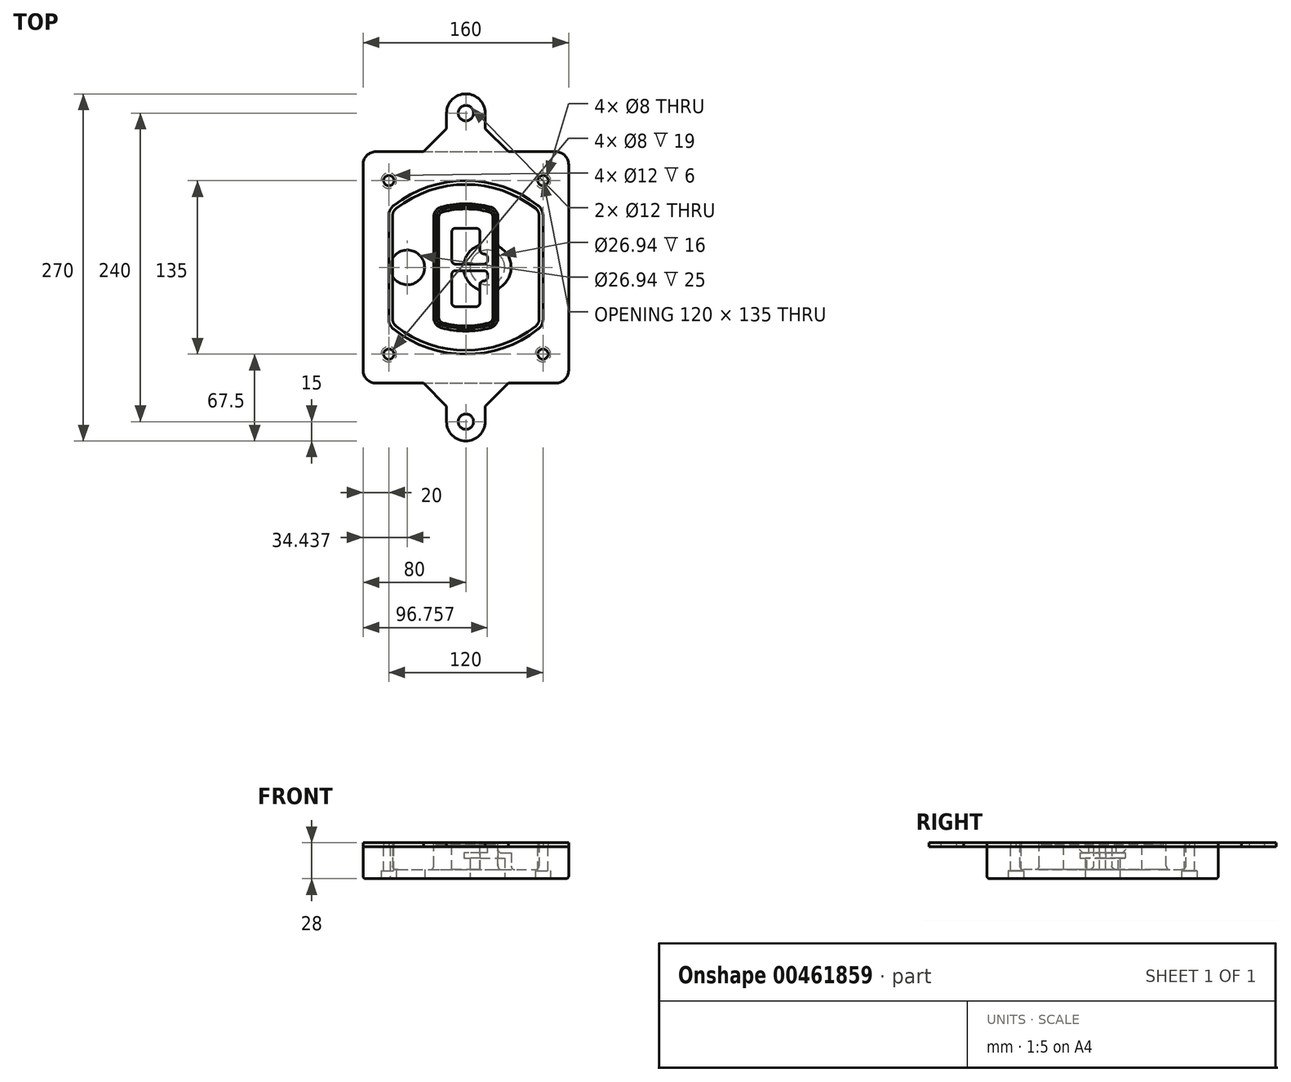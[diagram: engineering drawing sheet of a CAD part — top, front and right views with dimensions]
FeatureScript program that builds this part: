
annotation { "Feature Type Name" : "Feature", "Feature Type Description" : "" }
export const myFeature = defineFeature(function(context is Context, id is Id, definition is map)
    precondition{}
    {
        {
            var Q0;
            Q0=qCreatedBy(makeId("Top.planeOp"),FACE);
            var sketch = newSketch(context, id + "F0", { "sketchPlane" : qUnion([Q0])});
            skPoint(sketch, "E0.rect.middle", {"position": v(0, 0) * mm});
            skLineSegment(sketch, "E1.bottom", {"start": v(-70, -90) * mm, "end": v(70, -90) * mm});
            skLineSegment(sketch, "E1.top", {"start": v(-70, 90) * mm, "end": v(70, 90) * mm});
            skLineSegment(sketch, "E1.left", {"start": v(-80, -80) * mm, "end": v(-80, 80) * mm});
            skLineSegment(sketch, "E1.right", {"start": v(80, -80) * mm, "end": v(80, 80) * mm});
            skLineSegment(sketch, "E2", {"start": v(-80, 90) * mm, "end": v(80, -90) * mm, "construction": true});
            skLineSegment(sketch, "E3", {"start": v(80, 90) * mm, "end": v(-80, -90) * mm, "construction": true});
            skCircle(sketch, "E4", {"center": v(-60, 67.5) * mm, "radius": 4 * mm});
            skCircle(sketch, "E5", {"center": v(60, 67.5) * mm, "radius": 4 * mm});
            skCircle(sketch, "E6", {"center": v(60, -67.5) * mm, "radius": 4 * mm});
            skCircle(sketch, "E7", {"center": v(-60, -67.5) * mm, "radius": 4 * mm});
            skLineSegment(sketch, "E8", {"start": v(-60, 67.5) * mm, "end": v(60, 67.5) * mm, "construction": true});
            skLineSegment(sketch, "E9", {"start": v(60, 67.5) * mm, "end": v(60, -67.5) * mm, "construction": true});
            skLineSegment(sketch, "E10", {"start": v(60, -67.5) * mm, "end": v(-60, -67.5) * mm, "construction": true});
            skLineSegment(sketch, "E11", {"start": v(-60, -67.5) * mm, "end": v(-60, 67.5) * mm, "construction": true});
            skLineSegment(sketch, "E12", {"start": v(-60, 40.3) * mm, "end": v(-60, -40.3) * mm});
            skLineSegment(sketch, "E13", {"start": v(60, 40.3) * mm, "end": v(60, -40.3) * mm});
            skArc(sketch, "E14", {"start": v(56.15, 48.18) * mm, "mid": v(0, 67.5) * mm, "end": v(-56.15, 48.18) * mm});
            skArc(sketch, "E15", {"start": v(-56.15, -48.18) * mm, "mid": v(0, -67.5) * mm, "end": v(56.15, -48.18) * mm});
            skLineSegment(sketch, "E16", {"start": v(-60, 0) * mm, "end": v(60, 0) * mm, "construction": true});
            skPoint(sketch, "E17.visualSharp", {"position": v(-60, -45) * mm});
            skArc(sketch, "E17.filletArc", {"start": v(-60, -40.3) * mm, "mid": v(-58.99, -44.68) * mm, "end": v(-56.15, -48.18) * mm});
            skPoint(sketch, "E18.visualSharp", {"position": v(-60, 45) * mm});
            skArc(sketch, "E18.filletArc", {"start": v(-56.15, 48.18) * mm, "mid": v(-58.99, 44.68) * mm, "end": v(-60, 40.3) * mm});
            skPoint(sketch, "E19.visualSharp", {"position": v(60, 45) * mm});
            skArc(sketch, "E19.filletArc", {"start": v(60, 40.3) * mm, "mid": v(58.99, 44.68) * mm, "end": v(56.15, 48.18) * mm});
            skPoint(sketch, "E20.visualSharp", {"position": v(60, -45) * mm});
            skArc(sketch, "E20.filletArc", {"start": v(56.15, -48.18) * mm, "mid": v(58.99, -44.68) * mm, "end": v(60, -40.3) * mm});
            skPoint(sketch, "E21.visualSharp", {"position": v(-80, 90) * mm});
            skArc(sketch, "E21.filletArc", {"start": v(-70, 90) * mm, "mid": v(-77.07, 87.07) * mm, "end": v(-80, 80) * mm});
            skPoint(sketch, "E22.visualSharp", {"position": v(80, 90) * mm});
            skArc(sketch, "E22.filletArc", {"start": v(80, 80) * mm, "mid": v(77.07, 87.07) * mm, "end": v(70, 90) * mm});
            skPoint(sketch, "E23.visualSharp", {"position": v(80, -90) * mm});
            skArc(sketch, "E23.filletArc", {"start": v(70, -90) * mm, "mid": v(77.07, -87.07) * mm, "end": v(80, -80) * mm});
            skPoint(sketch, "E24.visualSharp", {"position": v(-80, -90) * mm});
            skArc(sketch, "E24.filletArc", {"start": v(-80, -80) * mm, "mid": v(-77.07, -87.07) * mm, "end": v(-70, -90) * mm});
            skArc(sketch, "E25.0", {"start": v(57, 40.3) * mm, "mid": v(56.3, 43.36) * mm, "end": v(54.3, 45.81) * mm});
            skLineSegment(sketch, "E25.1", {"start": v(57, 40.3) * mm, "end": v(57, -40.3) * mm});
            skArc(sketch, "E25.2", {"start": v(54.3, -45.81) * mm, "mid": v(56.3, -43.36) * mm, "end": v(57, -40.3) * mm});
            skArc(sketch, "E25.3", {"start": v(-54.3, -45.81) * mm, "mid": v(0, -64.5) * mm, "end": v(54.3, -45.81) * mm});
            skArc(sketch, "E25.4", {"start": v(-57, -40.3) * mm, "mid": v(-56.3, -43.36) * mm, "end": v(-54.3, -45.81) * mm});
            skArc(sketch, "E25.5", {"start": v(54.3, 45.81) * mm, "mid": v(0, 64.5) * mm, "end": v(-54.3, 45.81) * mm});
            skLineSegment(sketch, "E25.6", {"start": v(-57, 40.3) * mm, "end": v(-57, -40.3) * mm});
            skArc(sketch, "E25.7", {"start": v(-54.3, 45.81) * mm, "mid": v(-56.3, 43.36) * mm, "end": v(-57, 40.3) * mm});
            skArc(sketch, "E26.0", {"start": v(-58.62, 51.33) * mm, "mid": v(-62.58, 46.43) * mm, "end": v(-64, 40.3) * mm});
            skArc(sketch, "E26.1", {"start": v(58.62, 51.33) * mm, "mid": v(0, 71.5) * mm, "end": v(-58.62, 51.33) * mm});
            skArc(sketch, "E26.2", {"start": v(64, 40.3) * mm, "mid": v(62.58, 46.43) * mm, "end": v(58.62, 51.33) * mm});
            skLineSegment(sketch, "E26.3", {"start": v(64, 40.3) * mm, "end": v(64, -40.3) * mm});
            skArc(sketch, "E26.4", {"start": v(58.62, -51.33) * mm, "mid": v(62.58, -46.43) * mm, "end": v(64, -40.3) * mm});
            skLineSegment(sketch, "E26.5", {"start": v(-64, 40.3) * mm, "end": v(-64, -40.3) * mm});
            skArc(sketch, "E26.6", {"start": v(-58.62, -51.33) * mm, "mid": v(0, -71.5) * mm, "end": v(58.62, -51.33) * mm});
            skArc(sketch, "E26.7", {"start": v(-64, -40.3) * mm, "mid": v(-62.58, -46.43) * mm, "end": v(-58.62, -51.33) * mm});
            skSolve(sketch);
        }
        {
            var Q0;
            Q0=makeQuery(id+"F0.imprint","IMPRINT",FACE,{"disambiguationData":[TD([[makeQuery(id+"F0.imprint","IMPRINT",EDGE,{"derivedFrom":sQuery(id+"F0.wireOp",EDGE,"E1.bottom")}),1.0]])]});
            var Q1;
            Q1=makeQuery(id+"F0.imprint","IMPRINT",FACE,{"disambiguationData":[TD([[makeQuery(id+"F0.imprint","IMPRINT",EDGE,{"derivedFrom":sQuery(id+"F0.wireOp",EDGE,"E12")}),1.0]])]});
            var Q2;
            Q2=makeQuery(id+"F0.imprint","IMPRINT",FACE,{"disambiguationData":[TD([[makeQuery(id+"F0.imprint","IMPRINT",EDGE,{"derivedFrom":sQuery(id+"F0.wireOp",EDGE,"E25.0")}),1.0]])]});
            var Q3;
            Q3=makeQuery(id+"F0.imprint","IMPRINT",FACE,{"disambiguationData":[TD([[makeQuery(id+"F0.imprint","IMPRINT",EDGE,{"derivedFrom":sQuery(id+"F0.wireOp",EDGE,"E12")}),-1.0]])]});
            extrude(context, id + "F1", {"entities" : qUnion([Q0, Q1, Q2, Q3]), "oppositeDirection" : true, "depth" : 25 * mm});
        }
        {
            var Q0;
            Q0=makeQuery(id+"F0.imprint","IMPRINT",FACE,{"disambiguationData":[TD([[makeQuery(id+"F0.imprint","IMPRINT",EDGE,{"derivedFrom":sQuery(id+"F0.wireOp",EDGE,"E12")}),1.0]])]});
            extrude(context, id + "F2", {"entities" : qUnion([Q0]), "operationType" : NewBodyOperationType.ADD, "depth" : 3 * mm});
        }
        {
            var Q0;
            Q0=makeQuery(id+"F0.imprint","IMPRINT",FACE,{"disambiguationData":[TD([[makeQuery(id+"F0.imprint","IMPRINT",EDGE,{"derivedFrom":sQuery(id+"F0.wireOp",EDGE,"E25.0")}),1.0]])]});
            extrude(context, id + "F3", {"entities" : qUnion([Q0]), "operationType" : NewBodyOperationType.REMOVE, "oppositeDirection" : true, "depth" : 18 * mm});
        }
        {
            var Q0;
            Q0=makeQuery(id+"F2.opExtrude","CAP_FACE",FACE,{"disambiguationData":[OSD([sQuery(id+"F0.wireOp",EDGE,"E12"),sQuery(id+"F0.wireOp",EDGE,"E13"),sQuery(id+"F0.wireOp",EDGE,"E14"),sQuery(id+"F0.wireOp",EDGE,"E15"),sQuery(id+"F0.wireOp",EDGE,"E17.filletArc"),sQuery(id+"F0.wireOp",EDGE,"E18.filletArc"),sQuery(id+"F0.wireOp",EDGE,"E19.filletArc"),sQuery(id+"F0.wireOp",EDGE,"E20.filletArc"),sQuery(id+"F0.wireOp",EDGE,"E25.0"),sQuery(id+"F0.wireOp",EDGE,"E25.1"),sQuery(id+"F0.wireOp",EDGE,"E25.2"),sQuery(id+"F0.wireOp",EDGE,"E25.3"),sQuery(id+"F0.wireOp",EDGE,"E25.4"),sQuery(id+"F0.wireOp",EDGE,"E25.5"),sQuery(id+"F0.wireOp",EDGE,"E25.6"),sQuery(id+"F0.wireOp",EDGE,"E25.7")])],"isStart":false});
            var sketch = newSketch(context, id + "F4", { "sketchPlane" : qUnion([Q0])});
            skArc(sketch, "E27.0", {"start": v(-19.08, -46.97) * mm, "mid": v(0, -49.5) * mm, "end": v(19.08, -46.97) * mm});
            skArc(sketch, "E28.0", {"start": v(19.08, 46.97) * mm, "mid": v(0, 49.5) * mm, "end": v(-19.08, 46.97) * mm});
            skLineSegment(sketch, "E29", {"start": v(-25, 39.25) * mm, "end": v(-25, -39.25) * mm});
            skLineSegment(sketch, "E30", {"start": v(25, 39.25) * mm, "end": v(25, -39.25) * mm});
            skLineSegment(sketch, "E31", {"start": v(-25, 45.1) * mm, "end": v(25, 45.1) * mm, "construction": true});
            skLineSegment(sketch, "E32", {"start": v(-25, -45.1) * mm, "end": v(25, -45.1) * mm, "construction": true});
            skPoint(sketch, "E33.visualSharp", {"position": v(-25, 45.1) * mm});
            skArc(sketch, "E33.filletArc", {"start": v(-19.08, 46.97) * mm, "mid": v(-23.35, 44.11) * mm, "end": v(-25, 39.25) * mm});
            skPoint(sketch, "E34.visualSharp", {"position": v(25, 45.1) * mm});
            skArc(sketch, "E34.filletArc", {"start": v(25, 39.25) * mm, "mid": v(23.35, 44.11) * mm, "end": v(19.08, 46.97) * mm});
            skPoint(sketch, "E35.visualSharp", {"position": v(25, -45.1) * mm});
            skArc(sketch, "E35.filletArc", {"start": v(19.08, -46.97) * mm, "mid": v(23.35, -44.11) * mm, "end": v(25, -39.25) * mm});
            skPoint(sketch, "E36.visualSharp", {"position": v(-25, -45.1) * mm});
            skArc(sketch, "E36.filletArc", {"start": v(-25, -39.25) * mm, "mid": v(-23.35, -44.11) * mm, "end": v(-19.08, -46.97) * mm});
            skArc(sketch, "E37.0", {"start": v(54.3, 45.81) * mm, "mid": v(0, 64.5) * mm, "end": v(-54.3, 45.81) * mm});
            skArc(sketch, "E37.1", {"start": v(-54.3, 45.81) * mm, "mid": v(-56.3, 43.36) * mm, "end": v(-57, 40.3) * mm});
            skLineSegment(sketch, "E37.2", {"start": v(-57, 40.3) * mm, "end": v(-57, -40.3) * mm});
            skArc(sketch, "E37.3", {"start": v(-57, -40.3) * mm, "mid": v(-56.3, -43.36) * mm, "end": v(-54.3, -45.81) * mm});
            skArc(sketch, "E37.4", {"start": v(-54.3, -45.81) * mm, "mid": v(0, -64.5) * mm, "end": v(54.3, -45.81) * mm});
            skArc(sketch, "E37.5", {"start": v(54.3, -45.81) * mm, "mid": v(56.3, -43.36) * mm, "end": v(57, -40.3) * mm});
            skLineSegment(sketch, "E37.6", {"start": v(57, 40.3) * mm, "end": v(57, -40.3) * mm});
            skArc(sketch, "E37.7", {"start": v(57, 40.3) * mm, "mid": v(56.3, 43.36) * mm, "end": v(54.3, 45.81) * mm});
            skLineSegment(sketch, "E38.0", {"start": v(23, 39.25) * mm, "end": v(23, -39.25) * mm});
            skArc(sketch, "E38.1", {"start": v(18.56, -45.04) * mm, "mid": v(21.76, -42.9) * mm, "end": v(23, -39.25) * mm});
            skArc(sketch, "E38.2", {"start": v(-18.56, -45.04) * mm, "mid": v(0, -47.5) * mm, "end": v(18.56, -45.04) * mm});
            skArc(sketch, "E38.3", {"start": v(-23, -39.25) * mm, "mid": v(-21.76, -42.9) * mm, "end": v(-18.56, -45.04) * mm});
            skLineSegment(sketch, "E38.4", {"start": v(-23, 39.25) * mm, "end": v(-23, -39.25) * mm});
            skArc(sketch, "E38.5", {"start": v(23, 39.25) * mm, "mid": v(21.76, 42.9) * mm, "end": v(18.56, 45.04) * mm});
            skArc(sketch, "E38.6", {"start": v(-18.56, 45.04) * mm, "mid": v(-21.76, 42.9) * mm, "end": v(-23, 39.25) * mm});
            skArc(sketch, "E38.7", {"start": v(18.56, 45.04) * mm, "mid": v(0, 47.5) * mm, "end": v(-18.56, 45.04) * mm});
            skArc(sketch, "E39.0", {"start": v(21, 39.25) * mm, "mid": v(20.18, 41.68) * mm, "end": v(18.04, 43.1) * mm});
            skLineSegment(sketch, "E39.1", {"start": v(21, 39.25) * mm, "end": v(21, -39.25) * mm});
            skArc(sketch, "E39.2", {"start": v(18.04, -43.1) * mm, "mid": v(20.18, -41.68) * mm, "end": v(21, -39.25) * mm});
            skArc(sketch, "E39.3", {"start": v(-18.04, -43.1) * mm, "mid": v(0, -45.5) * mm, "end": v(18.04, -43.1) * mm});
            skArc(sketch, "E39.4", {"start": v(-21, -39.25) * mm, "mid": v(-20.18, -41.68) * mm, "end": v(-18.04, -43.1) * mm});
            skArc(sketch, "E39.5", {"start": v(18.04, 43.1) * mm, "mid": v(0, 45.5) * mm, "end": v(-18.04, 43.1) * mm});
            skLineSegment(sketch, "E39.6", {"start": v(-21, 39.25) * mm, "end": v(-21, -39.25) * mm});
            skArc(sketch, "E39.7", {"start": v(-18.04, 43.1) * mm, "mid": v(-20.18, 41.68) * mm, "end": v(-21, 39.25) * mm});
            skLineSegment(sketch, "E40", {"start": v(-25, 0) * mm, "end": v(25, 0) * mm, "construction": true});
            skLineSegment(sketch, "E41", {"start": v(-11, 5.5) * mm, "end": v(-11, 27.5) * mm});
            skLineSegment(sketch, "E42", {"start": v(-8, 30.5) * mm, "end": v(8, 30.5) * mm});
            skLineSegment(sketch, "E43", {"start": v(11, 27.5) * mm, "end": v(11, 13.5) * mm});
            skLineSegment(sketch, "E44", {"start": v(14, 10.5) * mm, "end": v(14, 10.5) * mm});
            skLineSegment(sketch, "E45", {"start": v(17, 7.5) * mm, "end": v(17, 5.5) * mm});
            skLineSegment(sketch, "E46", {"start": v(14, 2.5) * mm, "end": v(-8, 2.5) * mm});
            skPoint(sketch, "E47.visualSharp", {"position": v(-11, 30.5) * mm});
            skArc(sketch, "E47.filletArc", {"start": v(-8, 30.5) * mm, "mid": v(-10.12, 29.62) * mm, "end": v(-11, 27.5) * mm});
            skPoint(sketch, "E48.visualSharp", {"position": v(11, 30.5) * mm});
            skArc(sketch, "E48.filletArc", {"start": v(11, 27.5) * mm, "mid": v(10.12, 29.62) * mm, "end": v(8, 30.5) * mm});
            skPoint(sketch, "E49.visualSharp", {"position": v(11, 10.5) * mm});
            skArc(sketch, "E49.filletArc", {"start": v(11, 13.5) * mm, "mid": v(11.88, 11.38) * mm, "end": v(14, 10.5) * mm});
            skPoint(sketch, "E50.visualSharp", {"position": v(17, 10.5) * mm});
            skArc(sketch, "E50.filletArc", {"start": v(17, 7.5) * mm, "mid": v(16.12, 9.62) * mm, "end": v(14, 10.5) * mm});
            skPoint(sketch, "E51.visualSharp", {"position": v(17, 2.5) * mm});
            skArc(sketch, "E51.filletArc", {"start": v(14, 2.5) * mm, "mid": v(16.12, 3.38) * mm, "end": v(17, 5.5) * mm});
            skPoint(sketch, "E52.visualSharp", {"position": v(-11, 2.5) * mm});
            skArc(sketch, "E52.filletArc", {"start": v(-11, 5.5) * mm, "mid": v(-10.12, 3.38) * mm, "end": v(-8, 2.5) * mm});
            skLineSegment(sketch, "E53.0.MirrorCS", {"start": v(14, -2.5) * mm, "end": v(-8, -2.5) * mm});
            skArc(sketch, "E54.0.MirrorCS", {"start": v(-11, -5.5) * mm, "mid": v(-10.12, -3.38) * mm, "end": v(-8, -2.5) * mm});
            skLineSegment(sketch, "E55.0.MirrorCS", {"start": v(-11, -5.5) * mm, "end": v(-11, -27.5) * mm});
            skArc(sketch, "E56.0.MirrorCS", {"start": v(-8, -30.5) * mm, "mid": v(-10.12, -29.62) * mm, "end": v(-11, -27.5) * mm});
            skLineSegment(sketch, "E57.0.MirrorCS", {"start": v(-8, -30.5) * mm, "end": v(8, -30.5) * mm});
            skArc(sketch, "E58.0.MirrorCS", {"start": v(11, -27.5) * mm, "mid": v(10.12, -29.62) * mm, "end": v(8, -30.5) * mm});
            skLineSegment(sketch, "E59.0.MirrorCS", {"start": v(11, -27.5) * mm, "end": v(11, -13.5) * mm});
            skArc(sketch, "E60.0.MirrorCS", {"start": v(11, -13.5) * mm, "mid": v(11.88, -11.38) * mm, "end": v(14, -10.5) * mm});
            skArc(sketch, "E61.0.MirrorCS", {"start": v(17, -7.5) * mm, "mid": v(16.12, -9.62) * mm, "end": v(14, -10.5) * mm});
            skLineSegment(sketch, "E62.0.MirrorCS", {"start": v(17, -7.5) * mm, "end": v(17, -5.5) * mm});
            skArc(sketch, "E63.0.MirrorCS", {"start": v(14, -2.5) * mm, "mid": v(16.12, -3.38) * mm, "end": v(17, -5.5) * mm});
            skSolve(sketch);
        }
        {
            var Q0;
            Q0=makeQuery(id+"F4.imprint","IMPRINT",FACE,{"disambiguationData":[TD([[makeQuery(id+"F4.imprint","IMPRINT",EDGE,{"derivedFrom":sQuery(id+"F4.wireOp",EDGE,"E27.0")}),1.0]])]});
            var Q1;
            Q1=makeQuery(id+"F4.imprint","IMPRINT",FACE,{"disambiguationData":[TD([[makeQuery(id+"F4.imprint","IMPRINT",EDGE,{"derivedFrom":sQuery(id+"F4.wireOp",EDGE,"E38.0")}),-1.0]])]});
            var Q2;
            Q2=makeQuery(id+"F4.imprint","IMPRINT",FACE,{"disambiguationData":[TD([[makeQuery(id+"F4.imprint","IMPRINT",EDGE,{"derivedFrom":sQuery(id+"F4.wireOp",EDGE,"E39.0")}),1.0]])]});
            extrude(context, id + "F5", {"entities" : qUnion([Q0, Q1, Q2]), "operationType" : NewBodyOperationType.ADD, "endBound" : BoundingType.UP_TO_NEXT, "oppositeDirection" : true, "depth" : 25 * mm});
        }
        {
            var Q0;
            Q0=makeQuery(id+"F4.imprint","IMPRINT",FACE,{"disambiguationData":[TD([[makeQuery(id+"F4.imprint","IMPRINT",EDGE,{"derivedFrom":sQuery(id+"F4.wireOp",EDGE,"E38.0")}),-1.0]])]});
            extrude(context, id + "F6", {"entities" : qUnion([Q0]), "operationType" : NewBodyOperationType.REMOVE, "oppositeDirection" : true, "depth" : 2 * mm});
        }
        {
            var Q0;
            Q0=makeQuery(id+"F1.opExtrude","CAP_FACE",FACE,{"disambiguationData":[OSD([sQuery(id+"F0.wireOp",EDGE,"E1.bottom"),sQuery(id+"F0.wireOp",EDGE,"E1.top"),sQuery(id+"F0.wireOp",EDGE,"E1.left"),sQuery(id+"F0.wireOp",EDGE,"E1.right"),sQuery(id+"F0.wireOp",EDGE,"E4"),sQuery(id+"F0.wireOp",EDGE,"E5"),sQuery(id+"F0.wireOp",EDGE,"E6"),sQuery(id+"F0.wireOp",EDGE,"E7"),sQuery(id+"F0.wireOp",EDGE,"E21.filletArc"),sQuery(id+"F0.wireOp",EDGE,"E22.filletArc"),sQuery(id+"F0.wireOp",EDGE,"E23.filletArc"),sQuery(id+"F0.wireOp",EDGE,"E24.filletArc")])],"isStart":false});
            var sketch = newSketch(context, id + "F7", { "sketchPlane" : qUnion([Q0])});
            skCircle(sketch, "E64", {"center": v(16.76, 0) * mm, "radius": 13.47 * mm});
            skCircle(sketch, "E65", {"center": v(-45.56, 0) * mm, "radius": 13.47 * mm});
            skLineSegment(sketch, "E66", {"start": v(80, 0) * mm, "end": v(-80, 0) * mm});
            skCircle(sketch, "E67", {"center": v(16.76, 0) * mm, "radius": 18.47 * mm});
            skCircle(sketch, "E68", {"center": v(60, -67.5) * mm, "radius": 6 * mm});
            skCircle(sketch, "E69", {"center": v(-60, -67.5) * mm, "radius": 6 * mm});
            skCircle(sketch, "E70", {"center": v(-60, 67.5) * mm, "radius": 6 * mm});
            skCircle(sketch, "E71", {"center": v(60, 67.5) * mm, "radius": 6 * mm});
            skSolve(sketch);
        }
        {
            var Q0;
            {var subQ1=sQuery(id+"F7.wireOp",EDGE,"E66");var subQ4=sQuery(id+"F7.wireOp",EDGE,"E64");var subQ6=makeQuery(id+"F7.imprint","INTERSECT",VERTEX,{"disambiguationData":[OD(0.0)],"derivedFrom":[subQ4,subQ1]});Q0=makeQuery(id+"F7.imprint","IMPRINT",FACE,{"disambiguationData":[TD([[makeQuery(id+"F7.imprint","IMPRINT",EDGE,{"disambiguationData":[TD([[subQ6,-1.0]])],"derivedFrom":subQ4}),-1.0]])]});}
            var Q1;
            {var subQ0=sQuery(id+"F7.wireOp",EDGE,"E66");var subQ1=sQuery(id+"F7.wireOp",EDGE,"E64");var subQ3=makeQuery(id+"F7.imprint","INTERSECT",VERTEX,{"disambiguationData":[OD(0.0)],"derivedFrom":[subQ1,subQ0]});Q1=makeQuery(id+"F7.imprint","IMPRINT",FACE,{"disambiguationData":[TD([[makeQuery(id+"F7.imprint","IMPRINT",EDGE,{"disambiguationData":[TD([[subQ3,-1.0]])],"derivedFrom":subQ1}),1.0]])]});}
            var Q2;
            {var subQ0=sQuery(id+"F7.wireOp",EDGE,"E66");var subQ1=sQuery(id+"F7.wireOp",EDGE,"E64");var subQ3=makeQuery(id+"F7.imprint","INTERSECT",VERTEX,{"disambiguationData":[OD(0.0)],"derivedFrom":[subQ1,subQ0]});Q2=makeQuery(id+"F7.imprint","IMPRINT",FACE,{"disambiguationData":[TD([[makeQuery(id+"F7.imprint","IMPRINT",EDGE,{"disambiguationData":[TD([[subQ3,1.0]])],"derivedFrom":subQ1}),1.0]])]});}
            var Q3;
            {var subQ1=sQuery(id+"F7.wireOp",EDGE,"E66");var subQ4=sQuery(id+"F7.wireOp",EDGE,"E64");var subQ6=makeQuery(id+"F7.imprint","INTERSECT",VERTEX,{"disambiguationData":[OD(0.0)],"derivedFrom":[subQ4,subQ1]});Q3=makeQuery(id+"F7.imprint","IMPRINT",FACE,{"disambiguationData":[TD([[makeQuery(id+"F7.imprint","IMPRINT",EDGE,{"disambiguationData":[TD([[subQ6,1.0]])],"derivedFrom":subQ4}),-1.0]])]});}
            extrude(context, id + "F8", {"entities" : qUnion([Q0, Q1, Q2, Q3]), "operationType" : NewBodyOperationType.ADD, "oppositeDirection" : true, "depth" : 20 * mm});
        }
        {
            var Q0;
            {var subQ0=sQuery(id+"F7.wireOp",EDGE,"E66");var subQ1=sQuery(id+"F7.wireOp",EDGE,"E64");var subQ3=makeQuery(id+"F7.imprint","INTERSECT",VERTEX,{"disambiguationData":[OD(0.0)],"derivedFrom":[subQ1,subQ0]});Q0=makeQuery(id+"F7.imprint","IMPRINT",FACE,{"disambiguationData":[TD([[makeQuery(id+"F7.imprint","IMPRINT",EDGE,{"disambiguationData":[TD([[subQ3,-1.0]])],"derivedFrom":subQ1}),1.0]])]});}
            var Q1;
            {var subQ0=sQuery(id+"F7.wireOp",EDGE,"E66");var subQ1=sQuery(id+"F7.wireOp",EDGE,"E64");var subQ3=makeQuery(id+"F7.imprint","INTERSECT",VERTEX,{"disambiguationData":[OD(0.0)],"derivedFrom":[subQ1,subQ0]});Q1=makeQuery(id+"F7.imprint","IMPRINT",FACE,{"disambiguationData":[TD([[makeQuery(id+"F7.imprint","IMPRINT",EDGE,{"disambiguationData":[TD([[subQ3,1.0]])],"derivedFrom":subQ1}),1.0]])]});}
            extrude(context, id + "F9", {"entities" : qUnion([Q0, Q1]), "operationType" : NewBodyOperationType.REMOVE, "oppositeDirection" : true, "depth" : 16 * mm});
        }
        {
            var Q0;
            {var subQ0=sQuery(id+"F7.wireOp",EDGE,"E66");var subQ1=sQuery(id+"F7.wireOp",EDGE,"E65");var subQ3=makeQuery(id+"F7.imprint","INTERSECT",VERTEX,{"disambiguationData":[OD(0.0)],"derivedFrom":[subQ1,subQ0]});Q0=makeQuery(id+"F7.imprint","IMPRINT",FACE,{"disambiguationData":[TD([[makeQuery(id+"F7.imprint","IMPRINT",EDGE,{"disambiguationData":[TD([[subQ3,-1.0]])],"derivedFrom":subQ1}),1.0]])]});}
            var Q1;
            {var subQ0=sQuery(id+"F7.wireOp",EDGE,"E66");var subQ1=sQuery(id+"F7.wireOp",EDGE,"E65");var subQ3=makeQuery(id+"F7.imprint","INTERSECT",VERTEX,{"disambiguationData":[OD(0.0)],"derivedFrom":[subQ1,subQ0]});Q1=makeQuery(id+"F7.imprint","IMPRINT",FACE,{"disambiguationData":[TD([[makeQuery(id+"F7.imprint","IMPRINT",EDGE,{"disambiguationData":[TD([[subQ3,1.0]])],"derivedFrom":subQ1}),1.0]])]});}
            extrude(context, id + "F10", {"entities" : qUnion([Q0, Q1]), "operationType" : NewBodyOperationType.REMOVE, "oppositeDirection" : true, "depth" : 25 * mm});
        }
        {
            var Q0;
            Q0=makeQuery(id+"F7.imprint","IMPRINT",FACE,{"disambiguationData":[TD([[makeQuery(id+"F7.imprint","IMPRINT",EDGE,{"derivedFrom":sQuery(id+"F7.wireOp",EDGE,"E68")}),1.0]])]});
            var Q1;
            Q1=makeQuery(id+"F7.imprint","IMPRINT",FACE,{"disambiguationData":[TD([[makeQuery(id+"F7.imprint","IMPRINT",EDGE,{"derivedFrom":makeQuery(id+"F1.opExtrude","CAP_EDGE",EDGE,{"disambiguationData":[OSD([sQuery(id+"F0.wireOp",EDGE,"E5")])],"isStart":false})}),-1.0]])]});
            var Q2;
            Q2=makeQuery(id+"F7.imprint","IMPRINT",FACE,{"disambiguationData":[TD([[makeQuery(id+"F7.imprint","IMPRINT",EDGE,{"derivedFrom":sQuery(id+"F7.wireOp",EDGE,"E69")}),1.0]])]});
            var Q3;
            Q3=makeQuery(id+"F7.imprint","IMPRINT",FACE,{"disambiguationData":[TD([[makeQuery(id+"F7.imprint","IMPRINT",EDGE,{"derivedFrom":makeQuery(id+"F1.opExtrude","CAP_EDGE",EDGE,{"disambiguationData":[OSD([sQuery(id+"F0.wireOp",EDGE,"E4")])],"isStart":false})}),-1.0]])]});
            var Q4;
            Q4=makeQuery(id+"F7.imprint","IMPRINT",FACE,{"disambiguationData":[TD([[makeQuery(id+"F7.imprint","IMPRINT",EDGE,{"derivedFrom":sQuery(id+"F7.wireOp",EDGE,"E70")}),1.0]])]});
            var Q5;
            Q5=makeQuery(id+"F7.imprint","IMPRINT",FACE,{"disambiguationData":[TD([[makeQuery(id+"F7.imprint","IMPRINT",EDGE,{"derivedFrom":makeQuery(id+"F1.opExtrude","CAP_EDGE",EDGE,{"disambiguationData":[OSD([sQuery(id+"F0.wireOp",EDGE,"E7")])],"isStart":false})}),-1.0]])]});
            var Q6;
            Q6=makeQuery(id+"F7.imprint","IMPRINT",FACE,{"disambiguationData":[TD([[makeQuery(id+"F7.imprint","IMPRINT",EDGE,{"derivedFrom":sQuery(id+"F7.wireOp",EDGE,"E71")}),1.0]])]});
            var Q7;
            Q7=makeQuery(id+"F7.imprint","IMPRINT",FACE,{"disambiguationData":[TD([[makeQuery(id+"F7.imprint","IMPRINT",EDGE,{"derivedFrom":makeQuery(id+"F1.opExtrude","CAP_EDGE",EDGE,{"disambiguationData":[OSD([sQuery(id+"F0.wireOp",EDGE,"E6")])],"isStart":false})}),-1.0]])]});
            extrude(context, id + "F11", {"entities" : qUnion([Q0, Q1, Q2, Q3, Q4, Q5, Q6, Q7]), "operationType" : NewBodyOperationType.REMOVE, "oppositeDirection" : true, "depth" : 6 * mm});
        }
        {
            var Q0;
            Q0=makeQuery(id+"F9.boolean.opBoolean","COPY",FACE,{"derivedFrom":makeQuery(id+"F9.opExtrude","CAP_FACE",FACE,{"disambiguationData":[OSD([sQuery(id+"F7.wireOp",EDGE,"E64")])],"isStart":false})});
            var sketch = newSketch(context, id + "F12", { "sketchPlane" : qUnion([Q0])});
            skArc(sketch, "E72.0", {"start": v(11, 17.55) * mm, "mid": v(2.57, 11.82) * mm, "end": v(-1.54, 2.5) * mm});
            skArc(sketch, "E72.1", {"start": v(-1.54, -2.5) * mm, "mid": v(2.57, -11.82) * mm, "end": v(11, -17.55) * mm});
            skLineSegment(sketch, "E73", {"start": v(-1.54, -2.5) * mm, "end": v(14, -2.5) * mm});
            skLineSegment(sketch, "E74.0", {"start": v(14, 2.5) * mm, "end": v(-1.54, 2.5) * mm});
            skArc(sketch, "E74.1", {"start": v(14, 2.5) * mm, "mid": v(16.12, 3.38) * mm, "end": v(17, 5.5) * mm});
            skLineSegment(sketch, "E74.2", {"start": v(17, 7.5) * mm, "end": v(17, 5.5) * mm});
            skArc(sketch, "E74.3", {"start": v(17, 7.5) * mm, "mid": v(16.12, 9.62) * mm, "end": v(14, 10.5) * mm});
            skArc(sketch, "E74.4", {"start": v(11, 13.5) * mm, "mid": v(11.88, 11.38) * mm, "end": v(14, 10.5) * mm});
            skLineSegment(sketch, "E74.5", {"start": v(11, 17.55) * mm, "end": v(11, 13.5) * mm});
            skLineSegment(sketch, "E74.7", {"start": v(14, -2.5) * mm, "end": v(-1.54, -2.5) * mm});
            skArc(sketch, "E74.8", {"start": v(14, -2.5) * mm, "mid": v(16.12, -3.38) * mm, "end": v(17, -5.5) * mm});
            skLineSegment(sketch, "E74.9", {"start": v(17, -7.5) * mm, "end": v(17, -5.5) * mm});
            skArc(sketch, "E74.10", {"start": v(17, -7.5) * mm, "mid": v(16.12, -9.62) * mm, "end": v(14, -10.5) * mm});
            skArc(sketch, "E74.11", {"start": v(11, -13.5) * mm, "mid": v(11.88, -11.38) * mm, "end": v(14, -10.5) * mm});
            skLineSegment(sketch, "E74.12", {"start": v(11, -17.55) * mm, "end": v(11, -13.5) * mm});
            skPoint(sketch, "E75.orphan", {"position": v(11, -27.5) * mm});
            skPoint(sketch, "E76.orphan", {"position": v(-8, -2.5) * mm});
            skPoint(sketch, "E77.orphan", {"position": v(-8, 2.5) * mm});
            skPoint(sketch, "E78.orphan", {"position": v(11, 27.5) * mm});
            skSolve(sketch);
        }
        {
            var Q0;
            {var subQ7=sQuery(id+"F12.wireOp",EDGE,"E72.0");var subQ14=sQuery(id+"F12.wireOp",EDGE,"E72.1");var subQ16=sQuery(id+"F12.wireOp",EDGE,"E74.1");var subQ18=sQuery(id+"F12.wireOp",EDGE,"E74.8");Q0=qUnion([makeQuery(id+"F12.imprint","IMPRINT",FACE,{"disambiguationData":[TD([[makeQuery(id+"F12.imprint","IMPRINT",EDGE,{"derivedFrom":subQ7}),1.0]])]}),makeQuery(id+"F12.imprint","IMPRINT",FACE,{"disambiguationData":[TD([[makeQuery(id+"F12.imprint","IMPRINT",EDGE,{"derivedFrom":subQ14}),1.0]])]}),makeQuery(id+"F12.imprint","IMPRINT",FACE,{"disambiguationData":[TD([[makeQuery(id+"F12.imprint","IMPRINT",EDGE,{"derivedFrom":subQ16}),1.0]])]}),makeQuery(id+"F12.imprint","IMPRINT",FACE,{"disambiguationData":[TD([[makeQuery(id+"F12.imprint","IMPRINT",EDGE,{"derivedFrom":subQ18}),-1.0]])]})]);}
            var Q1;
            Q1=makeQuery(id+"F5.boolean.opBoolean","SPLIT",FACE,{"disambiguationData":[TD([makeQuery(id+"F5.opExtrude","SWEPT_FACE",FACE,{"disambiguationData":[OSD([sQuery(id+"F4.wireOp",EDGE,"E41")])]})])],"derivedFrom":makeQuery(id+"F3.boolean.opBoolean","COPY",FACE,{"derivedFrom":makeQuery(id+"F3.opExtrude","CAP_FACE",FACE,{"disambiguationData":[OSD([sQuery(id+"F0.wireOp",EDGE,"E25.0"),sQuery(id+"F0.wireOp",EDGE,"E25.1"),sQuery(id+"F0.wireOp",EDGE,"E25.2"),sQuery(id+"F0.wireOp",EDGE,"E25.3"),sQuery(id+"F0.wireOp",EDGE,"E25.4"),sQuery(id+"F0.wireOp",EDGE,"E25.5"),sQuery(id+"F0.wireOp",EDGE,"E25.6"),sQuery(id+"F0.wireOp",EDGE,"E25.7")])],"isStart":false})})});
            extrude(context, id + "F13", {"entities" : qUnion([Q0]), "operationType" : NewBodyOperationType.REMOVE, "endBound" : BoundingType.UP_TO_SURFACE, "endBoundEntityFace" : qUnion([Q1]), "depth" : 25 * mm});
        }
        {
            var Q0;
            Q0=makeQuery(id+"F3.boolean.opBoolean","COPY",EDGE,{"derivedFrom":makeQuery(id+"F3.opExtrude","CAP_EDGE",EDGE,{"disambiguationData":[OSD([sQuery(id+"F0.wireOp",EDGE,"E25.6")])],"isStart":false})});
            var Q1;
            Q1=makeQuery(id+"F8.boolean.opBoolean","INTERSECT",EDGE,{"derivedFrom":[makeQuery(id+"F5.opExtrude","SWEPT_FACE",FACE,{"disambiguationData":[OSD([sQuery(id+"F4.wireOp",EDGE,"E30")])]}),makeQuery(id+"F8.opExtrude","CAP_FACE",FACE,{"disambiguationData":[OSD([sQuery(id+"F7.wireOp",EDGE,"E67")])],"isStart":false})]});
            var Q2;
            Q2=makeQuery(id+"F8.boolean.opBoolean","INTERSECT",EDGE,{"disambiguationData":[OD(1.0)],"derivedFrom":[makeQuery(id+"F5.opExtrude","SWEPT_FACE",FACE,{"disambiguationData":[OSD([sQuery(id+"F4.wireOp",EDGE,"E30")])]}),makeQuery(id+"F8.opExtrude","SWEPT_FACE",FACE,{"disambiguationData":[OSD([sQuery(id+"F7.wireOp",EDGE,"E67")])]})]});
            var Q3;
            {var subQ0=sQuery(id+"F4.wireOp",EDGE,"E30");Q3=makeQuery(id+"F8.boolean.opBoolean","SPLIT",EDGE,{"disambiguationData":[TD([makeQuery(id+"F5.opExtrude","SWEPT_FACE",FACE,{"disambiguationData":[OSD([sQuery(id+"F4.wireOp",EDGE,"E35.filletArc")])]})])],"derivedFrom":makeQuery(id+"F5.opExtrude","CAP_EDGE",EDGE,{"disambiguationData":[OSD([subQ0])],"isStart":false})});}
            var Q4;
            {var subQ0=sQuery(id+"F0.wireOp",EDGE,"E25.7");var subQ1=sQuery(id+"F0.wireOp",EDGE,"E25.1");var subQ2=sQuery(id+"F0.wireOp",EDGE,"E25.6");var subQ3=sQuery(id+"F0.wireOp",EDGE,"E25.5");var subQ4=sQuery(id+"F0.wireOp",EDGE,"E25.4");var subQ5=sQuery(id+"F0.wireOp",EDGE,"E25.0");var subQ6=sQuery(id+"F0.wireOp",EDGE,"E25.2");var subQ7=sQuery(id+"F0.wireOp",EDGE,"E25.3");Q4=makeQuery(id+"F8.boolean.opBoolean","INTERSECT",EDGE,{"derivedFrom":[makeQuery(id+"F5.boolean.opBoolean","SPLIT",FACE,{"disambiguationData":[TD([makeQuery(id+"F2.opExtrude","SWEPT_FACE",FACE,{"disambiguationData":[OSD([subQ5])]})])],"derivedFrom":makeQuery(id+"F3.boolean.opBoolean","COPY",FACE,{"derivedFrom":makeQuery(id+"F3.opExtrude","CAP_FACE",FACE,{"disambiguationData":[OSD([subQ5,subQ1,subQ6,subQ7,subQ4,subQ3,subQ2,subQ0])],"isStart":false})})}),makeQuery(id+"F8.opExtrude","SWEPT_FACE",FACE,{"disambiguationData":[OSD([sQuery(id+"F7.wireOp",EDGE,"E67")])]})]});}
            var Q5;
            Q5=makeQuery(id+"F8.boolean.opBoolean","INTERSECT",EDGE,{"disambiguationData":[OD(0.0)],"derivedFrom":[makeQuery(id+"F5.opExtrude","SWEPT_FACE",FACE,{"disambiguationData":[OSD([sQuery(id+"F4.wireOp",EDGE,"E30")])]}),makeQuery(id+"F8.opExtrude","SWEPT_FACE",FACE,{"disambiguationData":[OSD([sQuery(id+"F7.wireOp",EDGE,"E67")])]})]});
            fillet(context, id + "F14", {"entities" : qUnion([Q0, Q1, Q2, Q3, Q4, Q5]), "radius" : 3 * mm, "tangentPropagation" : true, "allowEdgeOverflow" : false});
        }
        {
            var Q0;
            Q0=makeQuery(id+"F1.opExtrude","CAP_EDGE",EDGE,{"disambiguationData":[OSD([sQuery(id+"F0.wireOp",EDGE,"E1.bottom")])],"isStart":false});
            fillet(context, id + "F15", {"entities" : qUnion([Q0]), "radius" : 2 * mm, "tangentPropagation" : true, "allowEdgeOverflow" : false});
        }
        {
            var Q0;
            {var subQ0=sQuery(id+"F0.wireOp",EDGE,"E21.filletArc");var subQ1=sQuery(id+"F0.wireOp",EDGE,"E7");var subQ2=sQuery(id+"F0.wireOp",EDGE,"E6");var subQ3=sQuery(id+"F0.wireOp",EDGE,"E5");var subQ4=sQuery(id+"F0.wireOp",EDGE,"E4");var subQ5=sQuery(id+"F0.wireOp",EDGE,"E22.filletArc");var subQ6=sQuery(id+"F0.wireOp",EDGE,"E1.bottom");var subQ7=sQuery(id+"F0.wireOp",EDGE,"E1.right");var subQ8=sQuery(id+"F0.wireOp",EDGE,"E1.top");var subQ9=sQuery(id+"F0.wireOp",EDGE,"E1.left");var subQ10=sQuery(id+"F0.wireOp",EDGE,"E23.filletArc");var subQ11=sQuery(id+"F0.wireOp",EDGE,"E24.filletArc");Q0=makeQuery(id+"F2.boolean.opBoolean","SPLIT",FACE,{"disambiguationData":[TD([makeQuery(id+"F1.opExtrude","SWEPT_FACE",FACE,{"disambiguationData":[OSD([subQ6])]})])],"derivedFrom":makeQuery(id+"F1.opExtrude","CAP_FACE",FACE,{"disambiguationData":[OSD([subQ6,subQ8,subQ9,subQ7,subQ4,subQ3,subQ2,subQ1,subQ0,subQ5,subQ10,subQ11])],"isStart":true})});}
            var sketch = newSketch(context, id + "F16", { "sketchPlane" : qUnion([Q0])});
            skLineSegment(sketch, "E79", {"start": v(0, 90) * mm, "end": v(0, 120) * mm, "construction": true});
            skCircle(sketch, "E80", {"center": v(0, 120) * mm, "radius": 6 * mm});
            skLineSegment(sketch, "E81", {"start": v(-33, 90) * mm, "end": v(-15, 108) * mm});
            skLineSegment(sketch, "E82", {"start": v(33, 90) * mm, "end": v(15, 108) * mm});
            skLineSegment(sketch, "E83", {"start": v(-15, 108) * mm, "end": v(-15, 120) * mm});
            skLineSegment(sketch, "E84", {"start": v(15, 108) * mm, "end": v(15, 120) * mm});
            skArc(sketch, "E85", {"start": v(-15, 120) * mm, "mid": v(0, 135) * mm, "end": v(15, 120) * mm});
            skLineSegment(sketch, "E86", {"start": v(-80, 0) * mm, "end": v(80, 0) * mm, "construction": true});
            skLineSegment(sketch, "E87.MirrorCS", {"start": v(0, -90) * mm, "end": v(0, -120) * mm, "construction": true});
            skCircle(sketch, "E88.MirrorC", {"center": v(0, -120) * mm, "radius": 6 * mm});
            skLineSegment(sketch, "E89.MirrorCS", {"start": v(-33, -90) * mm, "end": v(-15, -108) * mm});
            skLineSegment(sketch, "E90.MirrorCS", {"start": v(33, -90) * mm, "end": v(15, -108) * mm});
            skLineSegment(sketch, "E91.MirrorCS", {"start": v(-15, -108) * mm, "end": v(-15, -120) * mm});
            skLineSegment(sketch, "E92.MirrorCS", {"start": v(15, -108) * mm, "end": v(15, -120) * mm});
            skArc(sketch, "E93.MirrorCS", {"start": v(-15, -120) * mm, "mid": v(0, -135) * mm, "end": v(15, -120) * mm});
            skSolve(sketch);
        }
        {
            var Q0;
            {var subQ1=sQuery(id+"F16.wireOp",EDGE,"E89.MirrorCS");Q0=makeQuery(id+"F16.imprint","IMPRINT",FACE,{"disambiguationData":[TD([[makeQuery(id+"F16.imprint","IMPRINT",EDGE,{"derivedFrom":subQ1}),1.0]])]});}
            var Q1;
            Q1=makeQuery(id+"F16.imprint","IMPRINT",FACE,{"disambiguationData":[TD([[makeQuery(id+"F16.imprint","IMPRINT",EDGE,{"derivedFrom":makeQuery(id+"F1.opExtrude","CAP_EDGE",EDGE,{"disambiguationData":[OSD([sQuery(id+"F0.wireOp",EDGE,"E1.left")])],"isStart":true})}),-1.0]])]});
            var Q2;
            Q2=makeQuery(id+"F16.imprint","IMPRINT",FACE,{"disambiguationData":[TD([[makeQuery(id+"F16.imprint","IMPRINT",EDGE,{"derivedFrom":sQuery(id+"F16.wireOp",EDGE,"E80")}),-1.0]])]});
            var Q3;
            Q3=makeQuery(id+"F2.opExtrude","CAP_FACE",FACE,{"disambiguationData":[OSD([sQuery(id+"F0.wireOp",EDGE,"E12"),sQuery(id+"F0.wireOp",EDGE,"E13"),sQuery(id+"F0.wireOp",EDGE,"E14"),sQuery(id+"F0.wireOp",EDGE,"E15"),sQuery(id+"F0.wireOp",EDGE,"E17.filletArc"),sQuery(id+"F0.wireOp",EDGE,"E18.filletArc"),sQuery(id+"F0.wireOp",EDGE,"E19.filletArc"),sQuery(id+"F0.wireOp",EDGE,"E20.filletArc"),sQuery(id+"F0.wireOp",EDGE,"E25.0"),sQuery(id+"F0.wireOp",EDGE,"E25.1"),sQuery(id+"F0.wireOp",EDGE,"E25.2"),sQuery(id+"F0.wireOp",EDGE,"E25.3"),sQuery(id+"F0.wireOp",EDGE,"E25.4"),sQuery(id+"F0.wireOp",EDGE,"E25.5"),sQuery(id+"F0.wireOp",EDGE,"E25.6"),sQuery(id+"F0.wireOp",EDGE,"E25.7")])],"isStart":false});
            extrude(context, id + "F17", {"entities" : qUnion([Q0, Q1, Q2]), "endBound" : BoundingType.UP_TO_SURFACE, "endBoundEntityFace" : qUnion([Q3]), "depth" : 25 * mm});
        }
    });
